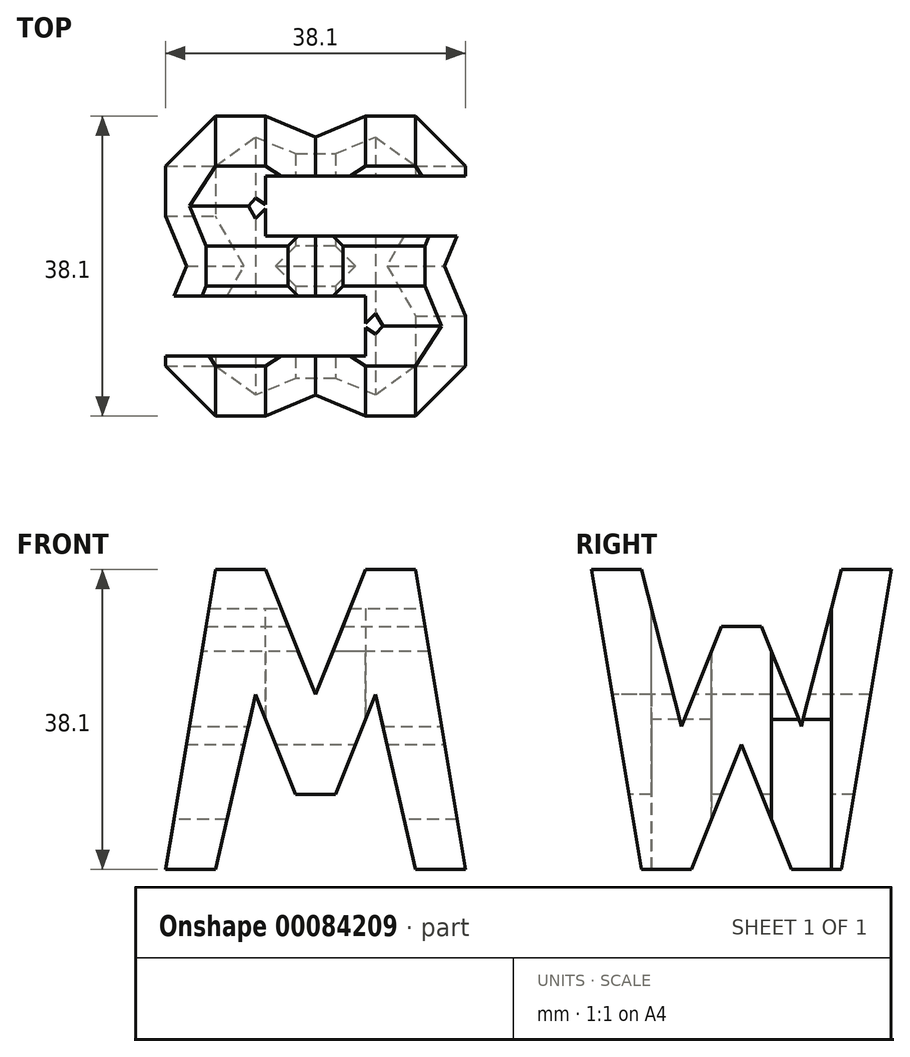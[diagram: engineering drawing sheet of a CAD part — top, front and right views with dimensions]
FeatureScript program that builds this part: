
annotation { "Feature Type Name" : "Feature", "Feature Type Description" : "" }
export const myFeature = defineFeature(function(context is Context, id is Id, definition is map)
    precondition{}
    {
        {
            var Q0;
            Q0=qCreatedBy(makeId("Front.planeOp"),FACE);
            var sketch = newSketch(context, id + "F0", { "sketchPlane" : qUnion([Q0])});
            skLineSegment(sketch, "E0", {"start": v(0, 0) * mm, "end": v(38.1, 0) * mm});
            skLineSegment(sketch, "E1", {"start": v(38.1, 0) * mm, "end": v(38.1, 38.1) * mm});
            skLineSegment(sketch, "E2", {"start": v(38.1, 38.1) * mm, "end": v(0, 38.1) * mm});
            skLineSegment(sketch, "E3", {"start": v(0, 38.1) * mm, "end": v(0, 0) * mm});
            skSolve(sketch);
        }
        {
            var Q0;
            Q0 = qSketchRegion(id + "F0", true);
            extrude(context, id + "F1", {"entities" : qUnion([Q0]), "depth" : 38.1 * mm});
        }
        {
            var Q0;
            Q0=qCreatedBy(makeId("Front.planeOp"),FACE);
            cPlane(context, id + "F2", {"entities" : qUnion([Q0]), "cplaneType" : CPlaneType.OFFSET, "offset" : 38.1 * mm, "width" : 152.4 * mm, "height" : 152.4 * mm});
        }
        {
            var Q0;
            Q0=qCreatedBy(makeId("Right.planeOp"),FACE);
            cPlane(context, id + "F3", {"entities" : qUnion([Q0]), "cplaneType" : CPlaneType.OFFSET, "offset" : 38.1 * mm, "width" : 152.4 * mm, "height" : 152.4 * mm});
        }
        {
            var Q0;
            Q0=qCreatedBy(makeId("Top.planeOp"),FACE);
            cPlane(context, id + "F4", {"entities" : qUnion([Q0]), "cplaneType" : CPlaneType.OFFSET, "offset" : 38.1 * mm, "width" : 152.4 * mm, "height" : 152.4 * mm});
        }
        {
            var Q0;
            Q0=qCreatedBy(id+"F3.planeOp",FACE);
            var sketch = newSketch(context, id + "F5", { "sketchPlane" : qUnion([Q0])});
            skLineSegment(sketch, "E4", {"start": v(0, 0) * mm, "end": v(0, 38.1) * mm});
            skLineSegment(sketch, "E5", {"start": v(0, 38.1) * mm, "end": v(-38.1, 38.1) * mm});
            skLineSegment(sketch, "E6", {"start": v(-38.1, 38.1) * mm, "end": v(-38.1, 0) * mm});
            skLineSegment(sketch, "E7", {"start": v(-38.1, 0) * mm, "end": v(0, 0) * mm});
            skLineSegment(sketch, "E8", {"start": v(-38.1, 38.1) * mm, "end": v(-31.75, 0) * mm});
            skLineSegment(sketch, "E9", {"start": v(-31.75, 0) * mm, "end": v(-25.4, 0) * mm});
            skLineSegment(sketch, "E10", {"start": v(-25.4, 0) * mm, "end": v(-19.05, 15.88) * mm});
            skLineSegment(sketch, "E11", {"start": v(-19.05, 15.88) * mm, "end": v(-12.7, 0) * mm});
            skLineSegment(sketch, "E12", {"start": v(-12.7, 0) * mm, "end": v(-6.35, 0) * mm});
            skLineSegment(sketch, "E13", {"start": v(-6.35, 0) * mm, "end": v(0, 38.1) * mm});
            skLineSegment(sketch, "E14", {"start": v(-31.75, 38.1) * mm, "end": v(-26.67, 18.2) * mm});
            skLineSegment(sketch, "E15", {"start": v(-26.67, 18.2) * mm, "end": v(-21.59, 30.9) * mm});
            skLineSegment(sketch, "E16", {"start": v(-21.59, 30.9) * mm, "end": v(-16.51, 30.9) * mm});
            skLineSegment(sketch, "E17", {"start": v(-16.51, 30.9) * mm, "end": v(-11.43, 18.2) * mm});
            skLineSegment(sketch, "E18", {"start": v(-11.43, 18.2) * mm, "end": v(-6.35, 38.1) * mm});
            skSolve(sketch);
        }
        {
            var Q0;
            {var subQ0=sQuery(id+"F5.wireOp",EDGE,"E6");Q0=makeQuery(id+"F5.imprint","IMPRINT",FACE,{"disambiguationData":[TD([[makeQuery(id+"F5.imprint","IMPRINT",EDGE,{"derivedFrom":subQ0}),1.0]])]});}
            var Q1;
            {var subQ0=sQuery(id+"F5.wireOp",EDGE,"E14");Q1=makeQuery(id+"F5.imprint","IMPRINT",FACE,{"disambiguationData":[TD([[makeQuery(id+"F5.imprint","IMPRINT",EDGE,{"derivedFrom":subQ0}),1.0]])]});}
            var Q2;
            {var subQ0=sQuery(id+"F5.wireOp",EDGE,"E10");Q2=makeQuery(id+"F5.imprint","IMPRINT",FACE,{"disambiguationData":[TD([[makeQuery(id+"F5.imprint","IMPRINT",EDGE,{"derivedFrom":subQ0}),-1.0]])]});}
            var Q3;
            {var subQ0=sQuery(id+"F5.wireOp",EDGE,"E4");Q3=makeQuery(id+"F5.imprint","IMPRINT",FACE,{"disambiguationData":[TD([[makeQuery(id+"F5.imprint","IMPRINT",EDGE,{"derivedFrom":subQ0}),1.0]])]});}
            extrude(context, id + "F6", {"entities" : qUnion([Q0, Q1, Q2, Q3]), "operationType" : NewBodyOperationType.REMOVE, "oppositeDirection" : true, "depth" : 38.1 * mm});
        }
        {
            var Q0;
            Q0=qCreatedBy(id+"F2.planeOp",FACE);
            var sketch = newSketch(context, id + "F7", { "sketchPlane" : qUnion([Q0])});
            skLineSegment(sketch, "E19", {"start": v(0, 0) * mm, "end": v(0, 38.1) * mm});
            skLineSegment(sketch, "E20", {"start": v(0, 38.1) * mm, "end": v(38.1, 38.1) * mm});
            skLineSegment(sketch, "E21", {"start": v(38.1, 38.1) * mm, "end": v(38.1, 0) * mm});
            skLineSegment(sketch, "E22", {"start": v(38.1, 0) * mm, "end": v(0, 0) * mm});
            skLineSegment(sketch, "E23", {"start": v(0, 0) * mm, "end": v(6.35, 38.1) * mm});
            skLineSegment(sketch, "E24", {"start": v(6.35, 38.1) * mm, "end": v(12.7, 38.1) * mm});
            skLineSegment(sketch, "E25", {"start": v(12.7, 38.1) * mm, "end": v(19.05, 22.22) * mm});
            skLineSegment(sketch, "E26", {"start": v(19.05, 22.23) * mm, "end": v(25.4, 38.1) * mm});
            skLineSegment(sketch, "E27", {"start": v(25.4, 38.1) * mm, "end": v(31.75, 38.1) * mm});
            skLineSegment(sketch, "E28", {"start": v(31.75, 38.1) * mm, "end": v(38.1, 0) * mm});
            skLineSegment(sketch, "E29", {"start": v(31.75, 0) * mm, "end": v(26.67, 22.23) * mm});
            skLineSegment(sketch, "E30", {"start": v(26.67, 22.23) * mm, "end": v(21.59, 9.52) * mm});
            skLineSegment(sketch, "E31", {"start": v(21.59, 9.53) * mm, "end": v(16.51, 9.53) * mm});
            skLineSegment(sketch, "E32", {"start": v(16.51, 9.52) * mm, "end": v(11.43, 22.23) * mm});
            skLineSegment(sketch, "E33", {"start": v(11.43, 22.23) * mm, "end": v(6.35, 0) * mm});
            skLineSegment(sketch, "E34", {"start": v(6.35, 0) * mm, "end": v(0, 0) * mm});
            skSolve(sketch);
        }
        {
            var Q0;
            {var subQ0=sQuery(id+"F7.wireOp",EDGE,"E19");Q0=makeQuery(id+"F7.imprint","IMPRINT",FACE,{"disambiguationData":[TD([[makeQuery(id+"F7.imprint","IMPRINT",EDGE,{"derivedFrom":subQ0}),-1.0]])]});}
            var Q1;
            {var subQ0=sQuery(id+"F7.wireOp",EDGE,"E25");Q1=makeQuery(id+"F7.imprint","IMPRINT",FACE,{"disambiguationData":[TD([[makeQuery(id+"F7.imprint","IMPRINT",EDGE,{"derivedFrom":subQ0}),1.0]])]});}
            var Q2;
            {var subQ0=sQuery(id+"F7.wireOp",EDGE,"E21");Q2=makeQuery(id+"F7.imprint","IMPRINT",FACE,{"disambiguationData":[TD([[makeQuery(id+"F7.imprint","IMPRINT",EDGE,{"derivedFrom":subQ0}),-1.0]])]});}
            var Q3;
            {var subQ0=sQuery(id+"F7.wireOp",EDGE,"E29");Q3=makeQuery(id+"F7.imprint","IMPRINT",FACE,{"disambiguationData":[TD([[makeQuery(id+"F7.imprint","IMPRINT",EDGE,{"derivedFrom":subQ0}),1.0]])]});}
            extrude(context, id + "F8", {"entities" : qUnion([Q0, Q1, Q2, Q3]), "operationType" : NewBodyOperationType.REMOVE, "oppositeDirection" : true, "depth" : 38.1 * mm});
        }
        {
            var Q0;
            Q0=qCreatedBy(id+"F4.planeOp",FACE);
            var sketch = newSketch(context, id + "F9", { "sketchPlane" : qUnion([Q0])});
            skLineSegment(sketch, "E35", {"start": v(0, 0) * mm, "end": v(0, -38.1) * mm});
            skLineSegment(sketch, "E36", {"start": v(0, -38.1) * mm, "end": v(38.1, -38.1) * mm});
            skLineSegment(sketch, "E37", {"start": v(38.1, -38.1) * mm, "end": v(38.1, 0) * mm});
            skLineSegment(sketch, "E38", {"start": v(38.1, 0) * mm, "end": v(0, 0) * mm});
            skLineSegment(sketch, "E39", {"start": v(38.1, -7.62) * mm, "end": v(12.7, -7.62) * mm});
            skLineSegment(sketch, "E40", {"start": v(12.7, -7.62) * mm, "end": v(12.7, -15.24) * mm});
            skLineSegment(sketch, "E41", {"start": v(12.7, -15.24) * mm, "end": v(38.1, -15.24) * mm});
            skLineSegment(sketch, "E42", {"start": v(0, -22.86) * mm, "end": v(25.4, -22.86) * mm});
            skLineSegment(sketch, "E43", {"start": v(25.4, -22.86) * mm, "end": v(25.4, -30.48) * mm});
            skLineSegment(sketch, "E44", {"start": v(25.4, -30.48) * mm, "end": v(0, -30.48) * mm});
            skSolve(sketch);
        }
        {
            var Q0;
            {var subQ0=sQuery(id+"F9.wireOp",EDGE,"E42");Q0=makeQuery(id+"F9.imprint","IMPRINT",FACE,{"disambiguationData":[TD([[makeQuery(id+"F9.imprint","IMPRINT",EDGE,{"derivedFrom":subQ0}),-1.0]])]});}
            var Q1;
            {var subQ0=sQuery(id+"F9.wireOp",EDGE,"E39");Q1=makeQuery(id+"F9.imprint","IMPRINT",FACE,{"disambiguationData":[TD([[makeQuery(id+"F9.imprint","IMPRINT",EDGE,{"derivedFrom":subQ0}),1.0]])]});}
            extrude(context, id + "F10", {"entities" : qUnion([Q0, Q1]), "operationType" : NewBodyOperationType.REMOVE, "oppositeDirection" : true, "depth" : 38.1 * mm});
        }
    });
